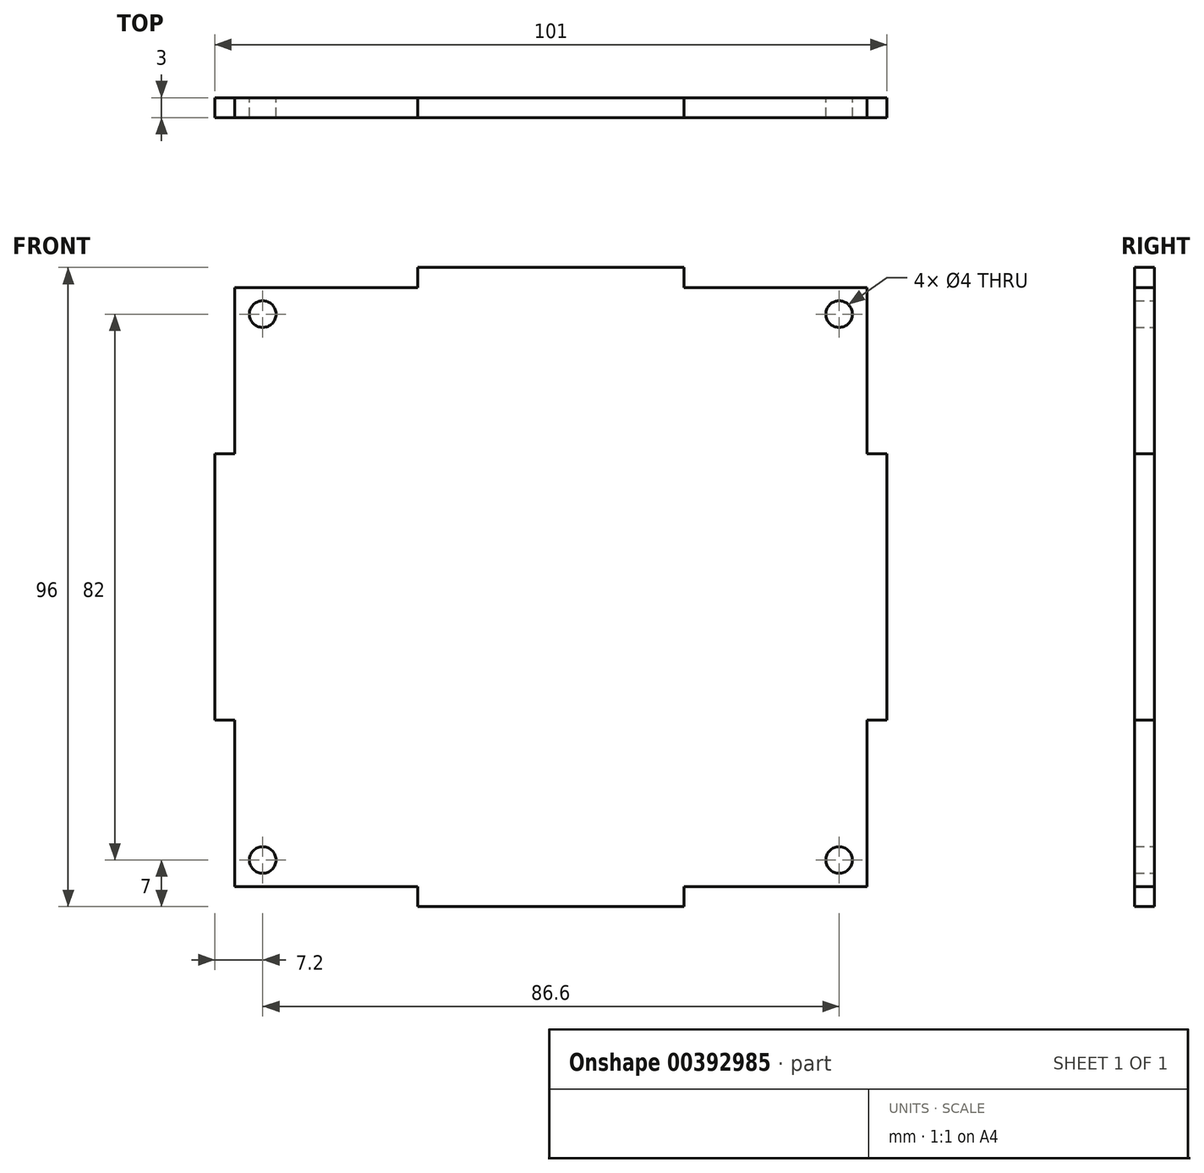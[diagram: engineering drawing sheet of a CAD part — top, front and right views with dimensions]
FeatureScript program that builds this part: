
annotation { "Feature Type Name" : "Feature", "Feature Type Description" : "" }
export const myFeature = defineFeature(function(context is Context, id is Id, definition is map)
    precondition{}
    {
        {
            var Q0;
            Q0=qCreatedBy(makeId("Front.planeOp"),FACE);
            var sketch = newSketch(context, id + "F0", { "sketchPlane" : qUnion([Q0])});
            skLineSegment(sketch, "E0", {"start": v(-50.5, 0) * mm, "end": v(-50.5, 20) * mm});
            skLineSegment(sketch, "E1", {"start": v(-50.5, 20) * mm, "end": v(-47.5, 20) * mm});
            skLineSegment(sketch, "E2", {"start": v(-47.5, 20) * mm, "end": v(-47.5, 45) * mm});
            skLineSegment(sketch, "E3", {"start": v(-47.5, 45) * mm, "end": v(-20, 45) * mm});
            skLineSegment(sketch, "E4", {"start": v(-20, 45) * mm, "end": v(-20, 48) * mm});
            skLineSegment(sketch, "E5", {"start": v(-20, 48) * mm, "end": v(0, 48) * mm});
            skLineSegment(sketch, "E6", {"start": v(-50.5, 0) * mm, "end": v(0, 0) * mm, "construction": true});
            skLineSegment(sketch, "E7", {"start": v(0, 0) * mm, "end": v(0, 48) * mm, "construction": true});
            skLineSegment(sketch, "E8.MirrorCS", {"start": v(50.5, 20) * mm, "end": v(47.5, 20) * mm});
            skLineSegment(sketch, "E9.MirrorCS", {"start": v(47.5, 20) * mm, "end": v(47.5, 45) * mm});
            skLineSegment(sketch, "E10.MirrorCS", {"start": v(47.5, 45) * mm, "end": v(20, 45) * mm});
            skLineSegment(sketch, "E11.MirrorCS", {"start": v(20, 45) * mm, "end": v(20, 48) * mm});
            skLineSegment(sketch, "E12.MirrorCS", {"start": v(50.5, 0) * mm, "end": v(50.5, 20) * mm});
            skLineSegment(sketch, "E13.MirrorCS", {"start": v(20, 48) * mm, "end": v(0, 48) * mm});
            skLineSegment(sketch, "E14.MirrorCS", {"start": v(50.5, -20) * mm, "end": v(47.5, -20) * mm});
            skLineSegment(sketch, "E15.MirrorCS", {"start": v(-20, -48) * mm, "end": v(0, -48) * mm});
            skLineSegment(sketch, "E16.MirrorCS", {"start": v(-50.5, 0) * mm, "end": v(-50.5, -20) * mm});
            skLineSegment(sketch, "E17.MirrorCS", {"start": v(47.5, -45) * mm, "end": v(20, -45) * mm});
            skLineSegment(sketch, "E18.MirrorCS", {"start": v(-50.5, -20) * mm, "end": v(-47.5, -20) * mm});
            skLineSegment(sketch, "E19.MirrorCS", {"start": v(-47.5, -20) * mm, "end": v(-47.5, -45) * mm});
            skLineSegment(sketch, "E20.MirrorCS", {"start": v(47.5, -20) * mm, "end": v(47.5, -45) * mm});
            skLineSegment(sketch, "E21.MirrorCS", {"start": v(20, -45) * mm, "end": v(20, -48) * mm});
            skLineSegment(sketch, "E22.MirrorCS", {"start": v(20, -48) * mm, "end": v(0, -48) * mm});
            skLineSegment(sketch, "E23.MirrorCS", {"start": v(-20, -45) * mm, "end": v(-20, -48) * mm});
            skLineSegment(sketch, "E24.MirrorCS", {"start": v(50.5, 0) * mm, "end": v(50.5, -20) * mm});
            skLineSegment(sketch, "E25.MirrorCS", {"start": v(-47.5, -45) * mm, "end": v(-20, -45) * mm});
            skCircle(sketch, "E26", {"center": v(-43.3, 41) * mm, "radius": 2 * mm});
            skLineSegment(sketch, "E27.MirrorCS", {"start": v(50.5, 0) * mm, "end": v(0, 0) * mm, "construction": true});
            skCircle(sketch, "E28.MirrorC", {"center": v(43.3, 41) * mm, "radius": 2 * mm});
            skCircle(sketch, "E29.MirrorC", {"center": v(-43.3, -41) * mm, "radius": 2 * mm});
            skCircle(sketch, "E30.MirrorC", {"center": v(43.3, -41) * mm, "radius": 2 * mm});
            skSolve(sketch);
        }
        {
            var Q0;
            Q0=qSketchRegion(id+"F0",true);
            extrude(context, id + "F1", {"entities" : qUnion([Q0]), "depth" : 3 * mm});
        }
    });
